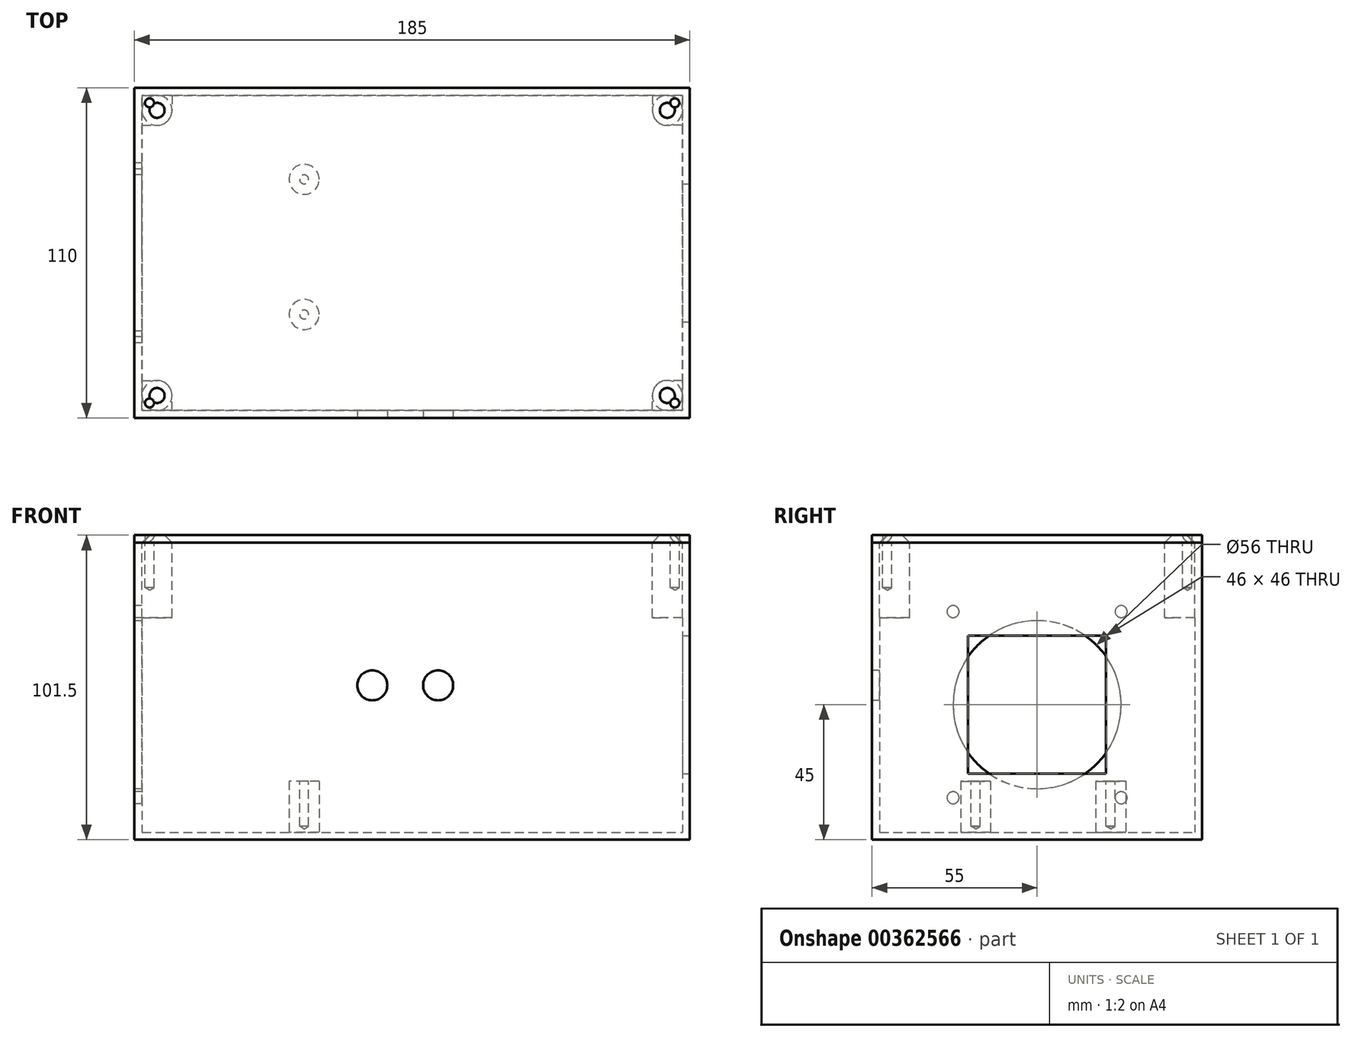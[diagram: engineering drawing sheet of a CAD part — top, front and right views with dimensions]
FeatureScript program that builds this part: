
annotation { "Feature Type Name" : "Feature", "Feature Type Description" : "" }
export const myFeature = defineFeature(function(context is Context, id is Id, definition is map)
    precondition{}
    {
        {
            var Q0;
            Q0=qCreatedBy(makeId("Top.planeOp"),FACE);
            var sketch = newSketch(context, id + "F0", { "sketchPlane" : qUnion([Q0])});
            skLineSegment(sketch, "E0.bottom", {"start": v(92.5, 55) * mm, "end": v(-92.5, 55) * mm});
            skLineSegment(sketch, "E0.top", {"start": v(92.5, -55) * mm, "end": v(-92.5, -55) * mm});
            skLineSegment(sketch, "E0.left", {"start": v(92.5, 55) * mm, "end": v(92.5, -55) * mm});
            skLineSegment(sketch, "E0.right", {"start": v(-92.5, 55) * mm, "end": v(-92.5, -55) * mm});
            skPoint(sketch, "E0.middle", {"position": v(0, 0) * mm});
            skLineSegment(sketch, "E1.bottom", {"start": v(90, 52.5) * mm, "end": v(-90, 52.5) * mm});
            skLineSegment(sketch, "E1.top", {"start": v(90, -52.5) * mm, "end": v(-90, -52.5) * mm});
            skLineSegment(sketch, "E1.left", {"start": v(90, 52.5) * mm, "end": v(90, -52.5) * mm});
            skLineSegment(sketch, "E1.right", {"start": v(-90, 52.5) * mm, "end": v(-90, -52.5) * mm});
            skSolve(sketch);
        }
        {
            var Q0;
            Q0=makeQuery(id+"F0.imprint","IMPRINT",FACE,{"disambiguationData":[TD([[makeQuery(id+"F0.imprint","IMPRINT",EDGE,{"derivedFrom":sQuery(id+"F0.wireOp",EDGE,"E0.bottom")}),1.0]])]});
            var Q1;
            Q1=makeQuery(id+"F0.imprint","IMPRINT",FACE,{"disambiguationData":[TD([[makeQuery(id+"F0.imprint","IMPRINT",EDGE,{"derivedFrom":sQuery(id+"F0.wireOp",EDGE,"E1.bottom")}),1.0]])]});
            extrude(context, id + "F1", {"entities" : qUnion([Q0, Q1]), "depth" : 2.5 * mm});
        }
        {
            var Q0;
            Q0=makeQuery(id+"F0.imprint","IMPRINT",FACE,{"disambiguationData":[TD([[makeQuery(id+"F0.imprint","IMPRINT",EDGE,{"derivedFrom":sQuery(id+"F0.wireOp",EDGE,"E0.bottom")}),1.0]])]});
            extrude(context, id + "F2", {"entities" : qUnion([Q0]), "operationType" : NewBodyOperationType.ADD, "depth" : 99 * mm});
        }
        {
            var Q0;
            Q0=makeQuery(id+"F1.opExtrude","SWEPT_BODY",BODY,{"disambiguationData":[OSD([sQuery(id+"F0.wireOp",EDGE,"E0.bottom"),sQuery(id+"F0.wireOp",EDGE,"E0.top"),sQuery(id+"F0.wireOp",EDGE,"E0.left"),sQuery(id+"F0.wireOp",EDGE,"E0.right")])]});
            transform(context, id + "F3", {"entities" : qUnion([Q0]), "transformType" : TransformType.TRANSLATION_3D, "dx" : 0 * mm, "dy" : 0 * mm, "dz" : -45 * mm, "makeCopy" : false});
        }
        {
            var Q0;
            {var subQ0=sQuery(id+"F0.wireOp",EDGE,"E0.left");Q0=makeQuery(id+"F2.boolean.opBoolean","MERGE",FACE,{"derivedFrom":[makeQuery(id+"F1.opExtrude","SWEPT_FACE",FACE,{"disambiguationData":[OSD([subQ0])]}),makeQuery(id+"F2.opExtrude","SWEPT_FACE",FACE,{"disambiguationData":[OSD([subQ0])]})]});}
            var sketch = newSketch(context, id + "F4", { "sketchPlane" : qUnion([Q0])});
            skLineSegment(sketch, "E2.bottom", {"start": v(23, 23) * mm, "end": v(-23, 23) * mm});
            skLineSegment(sketch, "E2.top", {"start": v(23, -23) * mm, "end": v(-23, -23) * mm});
            skLineSegment(sketch, "E2.left", {"start": v(23, 23) * mm, "end": v(23, -23) * mm});
            skLineSegment(sketch, "E2.right", {"start": v(-23, 23) * mm, "end": v(-23, -23) * mm});
            skPoint(sketch, "E2.middle", {"position": v(0, 0) * mm});
            skSolve(sketch);
        }
        {
            var Q0;
            Q0=makeQuery(id+"F4.imprint","IMPRINT",FACE,{"disambiguationData":[TD([[makeQuery(id+"F4.imprint","IMPRINT",EDGE,{"derivedFrom":sQuery(id+"F4.wireOp",EDGE,"E2.bottom")}),1.0]])]});
            extrude(context, id + "F5", {"entities" : qUnion([Q0]), "operationType" : NewBodyOperationType.REMOVE, "oppositeDirection" : true, "depth" : 7 * mm});
        }
        {
            var Q0;
            {var subQ0=sQuery(id+"F0.wireOp",EDGE,"E0.right");Q0=makeQuery(id+"F2.boolean.opBoolean","MERGE",FACE,{"derivedFrom":[makeQuery(id+"F1.opExtrude","SWEPT_FACE",FACE,{"disambiguationData":[OSD([subQ0])]}),makeQuery(id+"F2.opExtrude","SWEPT_FACE",FACE,{"disambiguationData":[OSD([subQ0])]})]});}
            var sketch = newSketch(context, id + "F6", { "sketchPlane" : qUnion([Q0])});
            skCircle(sketch, "E3", {"center": v(0, 0) * mm, "radius": 28 * mm});
            skLineSegment(sketch, "E4.bottom", {"start": v(-28, 31) * mm, "end": v(28, 31) * mm});
            skLineSegment(sketch, "E4.top", {"start": v(-28, -31) * mm, "end": v(28, -31) * mm});
            skLineSegment(sketch, "E4.left", {"start": v(-28, 31) * mm, "end": v(-28, -31) * mm});
            skLineSegment(sketch, "E4.right", {"start": v(28, 31) * mm, "end": v(28, -31) * mm});
            skSolve(sketch);
        }
        {
            var Q0;
            Q0=sQuery(id+"F6.wireOp",VERTEX,"E4.left.end");
            var Q1;
            Q1=sQuery(id+"F6.wireOp",VERTEX,"E4.left.start");
            var Q2;
            Q2=sQuery(id+"F6.wireOp",VERTEX,"E4.right.start");
            var Q3;
            Q3=sQuery(id+"F6.wireOp",VERTEX,"E4.right.end");
            var Q4;
            Q4=makeQuery(id+"F1.opExtrude","SWEPT_BODY",BODY,{"disambiguationData":[OSD([sQuery(id+"F0.wireOp",EDGE,"E0.bottom"),sQuery(id+"F0.wireOp",EDGE,"E0.top"),sQuery(id+"F0.wireOp",EDGE,"E0.left"),sQuery(id+"F0.wireOp",EDGE,"E0.right")])]});
            hole(context, id + "F7", {"style" : HoleStyle.SIMPLE, "endStyle" : HoleEndStyle.BLIND, "holeDiameter" : 4 * mm, "holeDepth" : 7 * mm, "isTappedThrough" : true, "tappedDepth" : 12 * mm, "tapClearance" : 3, "locations" : qUnion([Q0, Q1, Q2, Q3]), "scope" : qUnion([Q4])});
        }
        {
            var Q0;
            {var subQ0=sQuery(id+"F6.wireOp",EDGE,"E3");var subQ1=makeQuery(id+"F6.imprint","INTERSECT",VERTEX,{"derivedFrom":[subQ0,sQuery(id+"F6.wireOp",EDGE,"E4.bottom")]});Q0=makeQuery(id+"F6.imprint","IMPRINT",FACE,{"disambiguationData":[TD([[makeQuery(id+"F6.imprint","IMPRINT",EDGE,{"disambiguationData":[TD([[subQ1,1.0]])],"derivedFrom":subQ0}),1.0]])]});}
            extrude(context, id + "F8", {"entities" : qUnion([Q0]), "operationType" : NewBodyOperationType.REMOVE, "oppositeDirection" : true, "depth" : 7 * mm});
        }
        {
            var Q0;
            Q0=makeQuery(id+"F1.opExtrude","SWEPT_BODY",BODY,{"disambiguationData":[OSD([sQuery(id+"F0.wireOp",EDGE,"E0.bottom"),sQuery(id+"F0.wireOp",EDGE,"E0.top"),sQuery(id+"F0.wireOp",EDGE,"E0.left"),sQuery(id+"F0.wireOp",EDGE,"E0.right")])]});
            transform(context, id + "F9", {"entities" : qUnion([Q0]), "transformType" : TransformType.TRANSLATION_3D, "dx" : 0 * mm, "dy" : 0 * mm, "dz" : 45 * mm, "makeCopy" : false});
        }
        {
            var Q0;
            Q0=makeQuery(id+"F1.opExtrude","CAP_FACE",FACE,{"disambiguationData":[OSD([sQuery(id+"F0.wireOp",EDGE,"E0.bottom"),sQuery(id+"F0.wireOp",EDGE,"E0.top"),sQuery(id+"F0.wireOp",EDGE,"E0.left"),sQuery(id+"F0.wireOp",EDGE,"E0.right")])],"isStart":false});
            var sketch = newSketch(context, id + "F10", { "sketchPlane" : qUnion([Q0])});
            skCircle(sketch, "E5", {"center": v(-36, 24.5) * mm, "radius": 5 * mm});
            skCircle(sketch, "E6", {"center": v(-36, -20.5) * mm, "radius": 5 * mm});
            skSolve(sketch);
        }
        {
            var Q0;
            Q0=makeQuery(id+"F10.imprint","IMPRINT",FACE,{"disambiguationData":[TD([[makeQuery(id+"F10.imprint","IMPRINT",EDGE,{"derivedFrom":sQuery(id+"F10.wireOp",EDGE,"E5")}),1.0]])]});
            var Q1;
            Q1=makeQuery(id+"F10.imprint","IMPRINT",FACE,{"disambiguationData":[TD([[makeQuery(id+"F10.imprint","IMPRINT",EDGE,{"derivedFrom":sQuery(id+"F10.wireOp",EDGE,"E6")}),1.0]])]});
            extrude(context, id + "F11", {"entities" : qUnion([Q0, Q1]), "operationType" : NewBodyOperationType.ADD, "depth" : 17 * mm});
        }
        {
            var Q0;
            Q0=makeQuery(id+"F11.opExtrude","CAP_FACE",FACE,{"disambiguationData":[OSD([sQuery(id+"F10.wireOp",EDGE,"E5")])],"isStart":false});
            var sketch = newSketch(context, id + "F12", { "sketchPlane" : qUnion([Q0])});
            skPoint(sketch, "E7", {"position": v(-36, 24.5) * mm});
            skPoint(sketch, "E8", {"position": v(-36, -20.5) * mm});
            skSolve(sketch);
        }
        {
            var Q0;
            Q0=sQuery(id+"F12.wireOp",VERTEX,"E7");
            var Q1;
            Q1=sQuery(id+"F12.wireOp",VERTEX,"E8");
            var Q2;
            Q2=makeQuery(id+"F1.opExtrude","SWEPT_BODY",BODY,{"disambiguationData":[OSD([sQuery(id+"F0.wireOp",EDGE,"E0.bottom"),sQuery(id+"F0.wireOp",EDGE,"E0.top"),sQuery(id+"F0.wireOp",EDGE,"E0.left"),sQuery(id+"F0.wireOp",EDGE,"E0.right")])]});
            hole(context, id + "F13", {"style" : HoleStyle.SIMPLE, "endStyle" : HoleEndStyle.BLIND, "holeDiameter" : 3 * mm, "holeDepth" : 15 * mm, "isTappedThrough" : true, "tappedDepth" : 12 * mm, "tapClearance" : 3, "startFromSketch" : true, "locations" : qUnion([Q0, Q1]), "scope" : qUnion([Q2])});
        }
        {
            var Q0;
            {var subQ0=sQuery(id+"F0.wireOp",EDGE,"E0.top");Q0=makeQuery(id+"F2.boolean.opBoolean","MERGE",FACE,{"derivedFrom":[makeQuery(id+"F1.opExtrude","SWEPT_FACE",FACE,{"disambiguationData":[OSD([subQ0])]}),makeQuery(id+"F2.opExtrude","SWEPT_FACE",FACE,{"disambiguationData":[OSD([subQ0])]})]});}
            var sketch = newSketch(context, id + "F14", { "sketchPlane" : qUnion([Q0])});
            skPoint(sketch, "E9", {"position": v(-13.27, 51.45) * mm});
            skPoint(sketch, "E10", {"position": v(8.66, 51.45) * mm});
            skSolve(sketch);
        }
        {
            var Q0;
            Q0=sQuery(id+"F14.wireOp",VERTEX,"E9");
            var Q1;
            Q1=sQuery(id+"F14.wireOp",VERTEX,"E10");
            var Q2;
            Q2=makeQuery(id+"F1.opExtrude","SWEPT_BODY",BODY,{"disambiguationData":[OSD([sQuery(id+"F0.wireOp",EDGE,"E0.bottom"),sQuery(id+"F0.wireOp",EDGE,"E0.top"),sQuery(id+"F0.wireOp",EDGE,"E0.left"),sQuery(id+"F0.wireOp",EDGE,"E0.right")])]});
            hole(context, id + "F15", {"style" : HoleStyle.SIMPLE, "endStyle" : HoleEndStyle.BLIND, "holeDiameter" : 10 * mm, "holeDepth" : 10 * mm, "isTappedThrough" : true, "tappedDepth" : 12 * mm, "tapClearance" : 3, "startFromSketch" : true, "locations" : qUnion([Q0, Q1]), "scope" : qUnion([Q2])});
        }
        {
            var Q0;
            Q0=makeQuery(id+"F2.opExtrude","CAP_FACE",FACE,{"disambiguationData":[OSD([sQuery(id+"F0.wireOp",EDGE,"E0.bottom"),sQuery(id+"F0.wireOp",EDGE,"E0.top"),sQuery(id+"F0.wireOp",EDGE,"E0.left"),sQuery(id+"F0.wireOp",EDGE,"E0.right"),sQuery(id+"F0.wireOp",EDGE,"E1.bottom"),sQuery(id+"F0.wireOp",EDGE,"E1.top"),sQuery(id+"F0.wireOp",EDGE,"E1.left"),sQuery(id+"F0.wireOp",EDGE,"E1.right")])],"isStart":false});
            var sketch = newSketch(context, id + "F16", { "sketchPlane" : qUnion([Q0])});
            skLineSegment(sketch, "E11.0", {"start": v(-90, 52.5) * mm, "end": v(-90, -52.5) * mm, "construction": true});
            skLineSegment(sketch, "E11.1", {"start": v(90, 52.5) * mm, "end": v(-90, 52.5) * mm, "construction": true});
            skLineSegment(sketch, "E11.2", {"start": v(90, 52.5) * mm, "end": v(90, -52.5) * mm, "construction": true});
            skLineSegment(sketch, "E11.3", {"start": v(90, -52.5) * mm, "end": v(-90, -52.5) * mm, "construction": true});
            skLineSegment(sketch, "E12.bottom", {"start": v(-90, 52.5) * mm, "end": v(-80, 52.5) * mm});
            skLineSegment(sketch, "E12.top", {"start": v(-90, 42.5) * mm, "end": v(-80, 42.5) * mm});
            skLineSegment(sketch, "E12.left", {"start": v(-90, 52.5) * mm, "end": v(-90, 42.5) * mm});
            skLineSegment(sketch, "E12.right", {"start": v(-80, 52.5) * mm, "end": v(-80, 42.5) * mm});
            skLineSegment(sketch, "E13.bottom", {"start": v(-90, -52.5) * mm, "end": v(-80, -52.5) * mm});
            skLineSegment(sketch, "E13.top", {"start": v(-90, -42.5) * mm, "end": v(-80, -42.5) * mm});
            skLineSegment(sketch, "E13.left", {"start": v(-90, -52.5) * mm, "end": v(-90, -42.5) * mm});
            skLineSegment(sketch, "E13.right", {"start": v(-80, -52.5) * mm, "end": v(-80, -42.5) * mm});
            skLineSegment(sketch, "E14.bottom", {"start": v(90, 52.5) * mm, "end": v(80, 52.5) * mm});
            skLineSegment(sketch, "E14.top", {"start": v(90, 42.5) * mm, "end": v(80, 42.5) * mm});
            skLineSegment(sketch, "E14.left", {"start": v(90, 52.5) * mm, "end": v(90, 42.5) * mm});
            skLineSegment(sketch, "E14.right", {"start": v(80, 52.5) * mm, "end": v(80, 42.5) * mm});
            skLineSegment(sketch, "E15.bottom", {"start": v(90, -52.5) * mm, "end": v(80, -52.5) * mm});
            skLineSegment(sketch, "E15.top", {"start": v(90, -42.5) * mm, "end": v(80, -42.5) * mm});
            skLineSegment(sketch, "E15.left", {"start": v(90, -52.5) * mm, "end": v(90, -42.5) * mm});
            skLineSegment(sketch, "E15.right", {"start": v(80, -52.5) * mm, "end": v(80, -42.5) * mm});
            skLineSegment(sketch, "E16", {"start": v(-90, 0) * mm, "end": v(90, 0) * mm, "construction": true});
            skLineSegment(sketch, "E17", {"start": v(0, 52.5) * mm, "end": v(0, -52.5) * mm, "construction": true});
            skLineSegment(sketch, "E18", {"start": v(-90, 47.5) * mm, "end": v(-85, 52.5) * mm, "construction": true});
            skPoint(sketch, "E19", {"position": v(-87.5, 50) * mm});
            skPoint(sketch, "E20", {"position": v(87.5, 50) * mm});
            skPoint(sketch, "E21", {"position": v(87.5, -50) * mm});
            skPoint(sketch, "E22", {"position": v(-87.5, -50) * mm});
            skSolve(sketch);
        }
        {
            var Q0;
            Q0=makeQuery(id+"F16.imprint","IMPRINT",FACE,{"disambiguationData":[TD([[makeQuery(id+"F16.imprint","IMPRINT",EDGE,{"derivedFrom":sQuery(id+"F16.wireOp",EDGE,"E12.bottom")}),1.0]])]});
            var Q1;
            Q1=makeQuery(id+"F16.imprint","IMPRINT",FACE,{"disambiguationData":[TD([[makeQuery(id+"F16.imprint","IMPRINT",EDGE,{"derivedFrom":sQuery(id+"F16.wireOp",EDGE,"E13.bottom")}),-1.0]])]});
            var Q2;
            Q2=makeQuery(id+"F16.imprint","IMPRINT",FACE,{"disambiguationData":[TD([[makeQuery(id+"F16.imprint","IMPRINT",EDGE,{"derivedFrom":sQuery(id+"F16.wireOp",EDGE,"E15.bottom")}),-1.0]])]});
            var Q3;
            Q3=makeQuery(id+"F16.imprint","IMPRINT",FACE,{"disambiguationData":[TD([[makeQuery(id+"F16.imprint","IMPRINT",EDGE,{"derivedFrom":sQuery(id+"F16.wireOp",EDGE,"E14.bottom")}),1.0]])]});
            extrude(context, id + "F17", {"entities" : qUnion([Q0, Q1, Q2, Q3]), "operationType" : NewBodyOperationType.ADD, "oppositeDirection" : true, "depth" : 25 * mm});
        }
        {
            var Q0;
            Q0=makeQuery(id+"F17.opExtrude","SWEPT_EDGE",EDGE,{"disambiguationData":[OSD([sQuery(id+"F16.wireOp",EDGE,"E13.top"),sQuery(id+"F16.wireOp",EDGE,"E13.right")])]});
            var Q1;
            Q1=makeQuery(id+"F17.opExtrude","SWEPT_EDGE",EDGE,{"disambiguationData":[OSD([sQuery(id+"F16.wireOp",EDGE,"E12.top"),sQuery(id+"F16.wireOp",EDGE,"E12.right")])]});
            var Q2;
            Q2=makeQuery(id+"F17.opExtrude","SWEPT_EDGE",EDGE,{"disambiguationData":[OSD([sQuery(id+"F16.wireOp",EDGE,"E14.top"),sQuery(id+"F16.wireOp",EDGE,"E14.right")])]});
            var Q3;
            Q3=makeQuery(id+"F17.opExtrude","SWEPT_EDGE",EDGE,{"disambiguationData":[OSD([sQuery(id+"F16.wireOp",EDGE,"E15.top"),sQuery(id+"F16.wireOp",EDGE,"E15.right")])]});
            fillet(context, id + "F18", {"entities" : qUnion([Q0, Q1, Q2, Q3]), "radius" : 5 * mm, "tangentPropagation" : true, "allowEdgeOverflow" : false});
        }
        {
            var Q0;
            Q0=sQuery(id+"F16.wireOp",VERTEX,"E22");
            var Q1;
            Q1=sQuery(id+"F16.wireOp",VERTEX,"E19");
            var Q2;
            Q2=sQuery(id+"F16.wireOp",VERTEX,"E20");
            var Q3;
            Q3=sQuery(id+"F16.wireOp",VERTEX,"E21");
            var Q4;
            Q4=makeQuery(id+"F1.opExtrude","SWEPT_BODY",BODY,{"disambiguationData":[OSD([sQuery(id+"F0.wireOp",EDGE,"E0.bottom"),sQuery(id+"F0.wireOp",EDGE,"E0.top"),sQuery(id+"F0.wireOp",EDGE,"E0.left"),sQuery(id+"F0.wireOp",EDGE,"E0.right")])]});
            hole(context, id + "F19", {"style" : HoleStyle.SIMPLE, "endStyle" : HoleEndStyle.BLIND, "holeDiameter" : 3 * mm, "holeDepth" : 15 * mm, "isTappedThrough" : true, "tappedDepth" : 12 * mm, "tapClearance" : 3, "startFromSketch" : true, "locations" : qUnion([Q0, Q1, Q2, Q3]), "scope" : qUnion([Q4])});
        }
        {
            var Q0;
            Q0=makeQuery(id+"F17.boolean.opBoolean","MERGE",FACE,{"derivedFrom":[makeQuery(id+"F2.opExtrude","CAP_FACE",FACE,{"disambiguationData":[OSD([sQuery(id+"F0.wireOp",EDGE,"E0.bottom"),sQuery(id+"F0.wireOp",EDGE,"E0.top"),sQuery(id+"F0.wireOp",EDGE,"E0.left"),sQuery(id+"F0.wireOp",EDGE,"E0.right"),sQuery(id+"F0.wireOp",EDGE,"E1.bottom"),sQuery(id+"F0.wireOp",EDGE,"E1.top"),sQuery(id+"F0.wireOp",EDGE,"E1.left"),sQuery(id+"F0.wireOp",EDGE,"E1.right")])],"isStart":false}),makeQuery(id+"F17.opExtrude","CAP_FACE",FACE,{"disambiguationData":[OSD([sQuery(id+"F16.wireOp",EDGE,"E12.bottom"),sQuery(id+"F16.wireOp",EDGE,"E12.top"),sQuery(id+"F16.wireOp",EDGE,"E12.left"),sQuery(id+"F16.wireOp",EDGE,"E12.right")])],"isStart":true}),makeQuery(id+"F17.opExtrude","CAP_FACE",FACE,{"disambiguationData":[OSD([sQuery(id+"F16.wireOp",EDGE,"E13.bottom"),sQuery(id+"F16.wireOp",EDGE,"E13.top"),sQuery(id+"F16.wireOp",EDGE,"E13.left"),sQuery(id+"F16.wireOp",EDGE,"E13.right")])],"isStart":true}),makeQuery(id+"F17.opExtrude","CAP_FACE",FACE,{"disambiguationData":[OSD([sQuery(id+"F16.wireOp",EDGE,"E14.bottom"),sQuery(id+"F16.wireOp",EDGE,"E14.top"),sQuery(id+"F16.wireOp",EDGE,"E14.left"),sQuery(id+"F16.wireOp",EDGE,"E14.right")])],"isStart":true}),makeQuery(id+"F17.opExtrude","CAP_FACE",FACE,{"disambiguationData":[OSD([sQuery(id+"F16.wireOp",EDGE,"E15.bottom"),sQuery(id+"F16.wireOp",EDGE,"E15.top"),sQuery(id+"F16.wireOp",EDGE,"E15.left"),sQuery(id+"F16.wireOp",EDGE,"E15.right")])],"isStart":true})]});
            var sketch = newSketch(context, id + "F20", { "sketchPlane" : qUnion([Q0])});
            skLineSegment(sketch, "E23.0", {"start": v(-92.5, 55) * mm, "end": v(-92.5, -55) * mm});
            skLineSegment(sketch, "E23.1", {"start": v(92.5, 55) * mm, "end": v(-92.5, 55) * mm});
            skLineSegment(sketch, "E23.2", {"start": v(92.5, 55) * mm, "end": v(92.5, -55) * mm});
            skLineSegment(sketch, "E23.3", {"start": v(92.5, -55) * mm, "end": v(-92.5, -55) * mm});
            skLineSegment(sketch, "E23.4", {"start": v(80, -52.5) * mm, "end": v(-80, -52.5) * mm});
            skLineSegment(sketch, "E24.0", {"start": v(90, 42.5) * mm, "end": v(90, -42.5) * mm});
            skArc(sketch, "E24.1", {"start": v(85, -42.5) * mm, "mid": v(81.46, -43.96) * mm, "end": v(80, -47.5) * mm});
            skLineSegment(sketch, "E24.2", {"start": v(80, -52.5) * mm, "end": v(80, -47.5) * mm});
            skLineSegment(sketch, "E24.3", {"start": v(90, -42.5) * mm, "end": v(85, -42.5) * mm});
            skArc(sketch, "E24.4", {"start": v(80, 47.5) * mm, "mid": v(81.46, 43.96) * mm, "end": v(85, 42.5) * mm});
            skLineSegment(sketch, "E24.5", {"start": v(90, 42.5) * mm, "end": v(85, 42.5) * mm});
            skLineSegment(sketch, "E24.6", {"start": v(80, 52.5) * mm, "end": v(80, 47.5) * mm});
            skLineSegment(sketch, "E24.7", {"start": v(80, 52.5) * mm, "end": v(-80, 52.5) * mm});
            skLineSegment(sketch, "E25.0", {"start": v(-80, -52.5) * mm, "end": v(-80, -47.5) * mm});
            skArc(sketch, "E25.1", {"start": v(-80, -47.5) * mm, "mid": v(-81.46, -43.96) * mm, "end": v(-85, -42.5) * mm});
            skLineSegment(sketch, "E25.2", {"start": v(-90, -42.5) * mm, "end": v(-85, -42.5) * mm});
            skLineSegment(sketch, "E25.3", {"start": v(-90, 42.5) * mm, "end": v(-90, -42.5) * mm});
            skLineSegment(sketch, "E25.4", {"start": v(-80, 52.5) * mm, "end": v(-80, 47.5) * mm});
            skArc(sketch, "E25.5", {"start": v(-85, 42.5) * mm, "mid": v(-81.46, 43.96) * mm, "end": v(-80, 47.5) * mm});
            skLineSegment(sketch, "E25.6", {"start": v(-90, 42.5) * mm, "end": v(-85, 42.5) * mm});
            skSolve(sketch);
        }
        {
            var Q0;
            Q0=makeQuery(id+"F20.imprint","IMPRINT",FACE,{"disambiguationData":[TD([[makeQuery(id+"F20.imprint","IMPRINT",EDGE,{"derivedFrom":sQuery(id+"F20.wireOp",EDGE,"E23.4")}),-1.0]])]});
            var Q1;
            Q1=makeQuery(id+"F20.imprint","IMPRINT",FACE,{"disambiguationData":[TD([[makeQuery(id+"F20.imprint","IMPRINT",EDGE,{"derivedFrom":sQuery(id+"F20.wireOp",EDGE,"E23.0")}),1.0]])]});
            var Q2;
            Q2=makeQuery(id+"F20.imprint","IMPRINT",FACE,{"disambiguationData":[TD([[makeQuery(id+"F20.imprint","IMPRINT",EDGE,{"derivedFrom":makeQuery(id+"F19.hole-2.boolean.opBoolean","COPY",EDGE,{"derivedFrom":makeQuery(id+"F19.hole-2.opRevolve","SWEPT_EDGE",EDGE,{"disambiguationData":[OSD([sQuery(id+"F19.hole-2.sketch.wireOp",EDGE,"core_line_2"),sQuery(id+"F19.hole-2.sketch.wireOp",EDGE,"core_line_3")])]})})}),1.0]])]});
            var Q3;
            Q3=makeQuery(id+"F20.imprint","IMPRINT",FACE,{"disambiguationData":[TD([[makeQuery(id+"F20.imprint","IMPRINT",EDGE,{"derivedFrom":makeQuery(id+"F19.hole-3.boolean.opBoolean","COPY",EDGE,{"derivedFrom":makeQuery(id+"F19.hole-3.opRevolve","SWEPT_EDGE",EDGE,{"disambiguationData":[OSD([sQuery(id+"F19.hole-3.sketch.wireOp",EDGE,"core_line_2"),sQuery(id+"F19.hole-3.sketch.wireOp",EDGE,"core_line_3")])]})})}),1.0]])]});
            var Q4;
            Q4=makeQuery(id+"F20.imprint","IMPRINT",FACE,{"disambiguationData":[TD([[makeQuery(id+"F20.imprint","IMPRINT",EDGE,{"derivedFrom":makeQuery(id+"F19.hole-0.boolean.opBoolean","COPY",EDGE,{"derivedFrom":makeQuery(id+"F19.hole-0.opRevolve","SWEPT_EDGE",EDGE,{"disambiguationData":[OSD([sQuery(id+"F19.hole-0.sketch.wireOp",EDGE,"core_line_2"),sQuery(id+"F19.hole-0.sketch.wireOp",EDGE,"core_line_3")])]})})}),1.0]])]});
            var Q5;
            Q5=makeQuery(id+"F20.imprint","IMPRINT",FACE,{"disambiguationData":[TD([[makeQuery(id+"F20.imprint","IMPRINT",EDGE,{"derivedFrom":makeQuery(id+"F19.hole-1.boolean.opBoolean","COPY",EDGE,{"derivedFrom":makeQuery(id+"F19.hole-1.opRevolve","SWEPT_EDGE",EDGE,{"disambiguationData":[OSD([sQuery(id+"F19.hole-1.sketch.wireOp",EDGE,"core_line_2"),sQuery(id+"F19.hole-1.sketch.wireOp",EDGE,"core_line_3")])]})})}),1.0]])]});
            extrude(context, id + "F21", {"entities" : qUnion([Q0, Q1, Q2, Q3, Q4, Q5]), "depth" : 2.5 * mm});
        }
        {
            var Q0;
            Q0=sQuery(id+"F20.wireOp",VERTEX,"E25.1.center");
            var Q1;
            Q1=sQuery(id+"F20.wireOp",VERTEX,"E25.5.center");
            var Q2;
            Q2=sQuery(id+"F20.wireOp",VERTEX,"E24.4.center");
            var Q3;
            Q3=sQuery(id+"F20.wireOp",VERTEX,"E24.1.center");
            var Q4;
            Q4=makeQuery(id+"F21.opExtrude","SWEPT_BODY",BODY,{"disambiguationData":[OSD([sQuery(id+"F20.wireOp",EDGE,"E23.0"),sQuery(id+"F20.wireOp",EDGE,"E23.1"),sQuery(id+"F20.wireOp",EDGE,"E23.2"),sQuery(id+"F20.wireOp",EDGE,"E23.3")])]});
            hole(context, id + "F22", {"style" : HoleStyle.C_SINK, "endStyle" : HoleEndStyle.BLIND, "oppositeDirection" : true, "holeDiameter" : 3 * mm, "cSinkDiameter" : 10 * mm, "cSinkAngle" : 90 * degree, "holeDepth" : 15 * mm, "isTappedThrough" : true, "tappedDepth" : 12 * mm, "tapClearance" : 3, "startFromSketch" : true, "locations" : qUnion([Q0, Q1, Q2, Q3]), "scope" : qUnion([Q4])});
        }
    });
